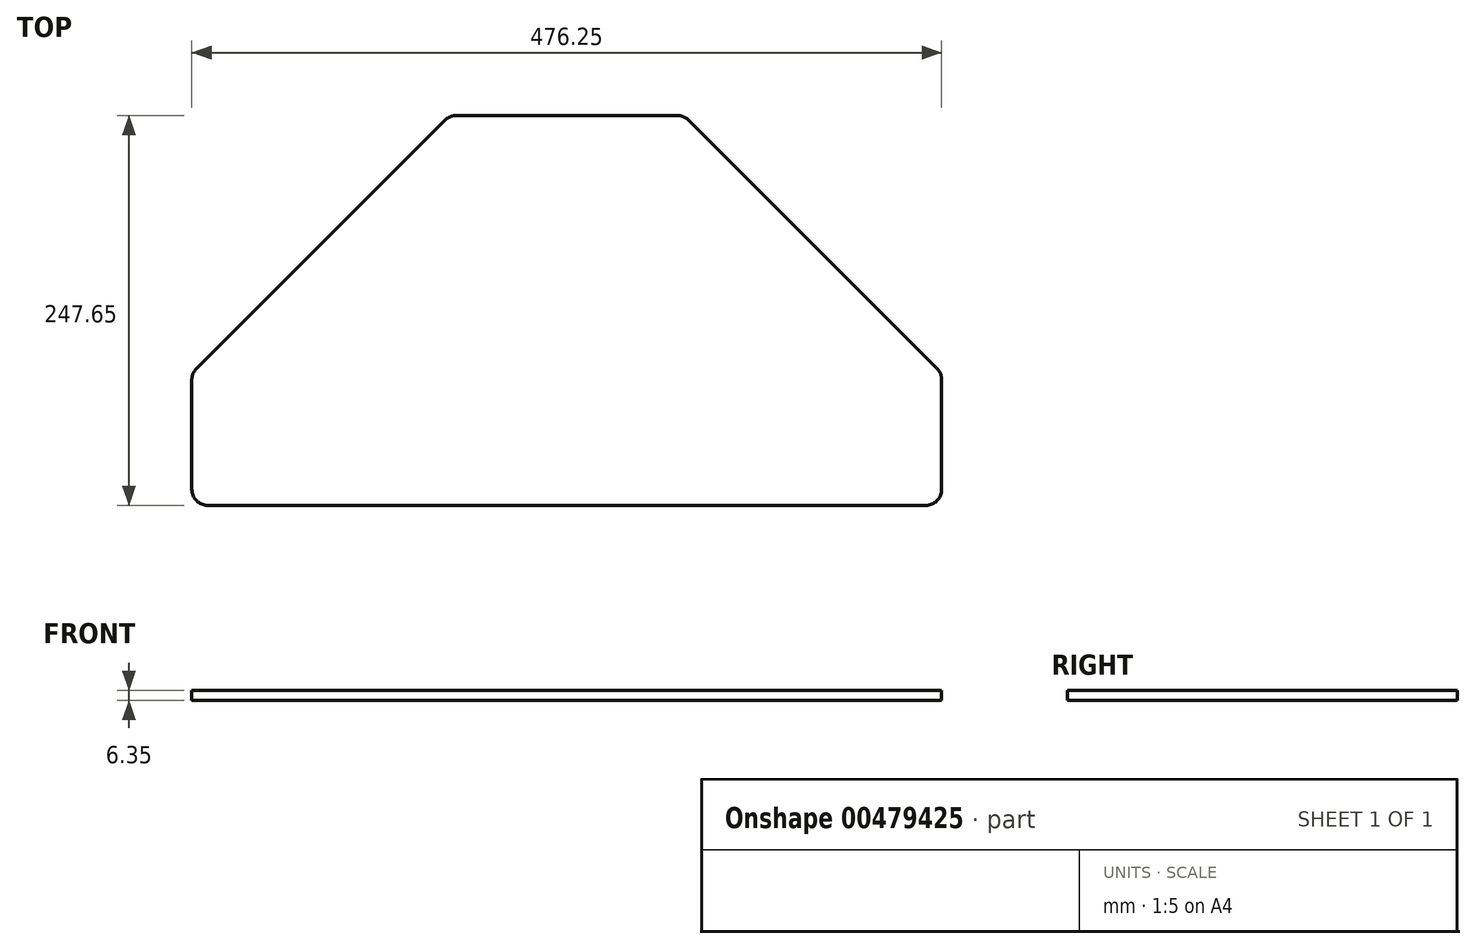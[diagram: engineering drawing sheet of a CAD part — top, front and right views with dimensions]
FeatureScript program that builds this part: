
annotation { "Feature Type Name" : "Feature", "Feature Type Description" : "" }
export const myFeature = defineFeature(function(context is Context, id is Id, definition is map)
    precondition{}
    {
        {
            var Q0;
            Q0=qCreatedBy(makeId("Top.planeOp"),FACE);
            var sketch = newSketch(context, id + "F0", { "sketchPlane" : qUnion([Q0]), "disableImprinting" : false});
            skLineSegment(sketch, "E0.bottom", {"start": v(0, 0) * mm, "end": v(476.25, 0) * mm});
            skLineSegment(sketch, "E0.top", {"start": v(0, 247.65) * mm, "end": v(476.25, 247.65) * mm});
            skLineSegment(sketch, "E0.left", {"start": v(0, 0) * mm, "end": v(0, 247.65) * mm});
            skLineSegment(sketch, "E0.right", {"start": v(476.25, 0) * mm, "end": v(476.25, 247.65) * mm});
            skLineSegment(sketch, "E1", {"start": v(0, 83.95) * mm, "end": v(476.25, 83.95) * mm});
            skPoint(sketch, "E2", {"position": v(163.7, 247.65) * mm});
            skPoint(sketch, "E3", {"position": v(312.55, 247.65) * mm});
            skLineSegment(sketch, "E4", {"start": v(0, 83.95) * mm, "end": v(163.7, 247.65) * mm});
            skLineSegment(sketch, "E5", {"start": v(312.55, 247.65) * mm, "end": v(476.25, 83.95) * mm});
            skSolve(sketch);
        }
        {
            var Q0;
            Q0=makeQuery(id+"F0.imprint","IMPRINT",FACE,{"disambiguationData":[TD([[makeQuery(id+"F0.imprint","IMPRINT",EDGE,{"derivedFrom":sQuery(id+"F0.wireOp",EDGE,"E1")}),1.0]])]});
            var Q1;
            {var subQ0=sQuery(id+"F0.wireOp",EDGE,"E0.bottom");Q1=makeQuery(id+"F0.imprint","IMPRINT",FACE,{"disambiguationData":[TD([[makeQuery(id+"F0.imprint","IMPRINT",EDGE,{"derivedFrom":subQ0}),1.0]])]});}
            extrude(context, id + "F1", {"entities" : qUnion([Q0, Q1]), "depth" : 6.35 * mm});
        }
        {
            var Q0;
            Q0=makeQuery(id+"F1.opExtrude","SWEPT_EDGE",EDGE,{"disambiguationData":[OSD([sQuery(id+"F0.wireOp",EDGE,"E0.top"),sQuery(id+"F0.wireOp",EDGE,"E4")])]});
            var Q1;
            Q1=makeQuery(id+"F1.opExtrude","SWEPT_EDGE",EDGE,{"disambiguationData":[OSD([sQuery(id+"F0.wireOp",EDGE,"E0.top"),sQuery(id+"F0.wireOp",EDGE,"E5")])]});
            var Q2;
            Q2=makeQuery(id+"F1.opExtrude","SWEPT_EDGE",EDGE,{"disambiguationData":[OSD([sQuery(id+"F0.wireOp",EDGE,"E0.right"),sQuery(id+"F0.wireOp",EDGE,"E1"),sQuery(id+"F0.wireOp",EDGE,"E5")])]});
            var Q3;
            Q3=makeQuery(id+"F1.opExtrude","SWEPT_EDGE",EDGE,{"disambiguationData":[OSD([sQuery(id+"F0.wireOp",EDGE,"E0.bottom"),sQuery(id+"F0.wireOp",EDGE,"E0.right")])]});
            var Q4;
            Q4=makeQuery(id+"F1.opExtrude","SWEPT_EDGE",EDGE,{"disambiguationData":[OSD([sQuery(id+"F0.wireOp",EDGE,"E0.bottom"),sQuery(id+"F0.wireOp",EDGE,"E0.left")])]});
            var Q5;
            Q5=makeQuery(id+"F1.opExtrude","SWEPT_EDGE",EDGE,{"disambiguationData":[OSD([sQuery(id+"F0.wireOp",EDGE,"E0.left"),sQuery(id+"F0.wireOp",EDGE,"E1"),sQuery(id+"F0.wireOp",EDGE,"E4")])]});
            fillet(context, id + "F2", {"entities" : qUnion([Q0, Q1, Q2, Q3, Q4, Q5]), "radius" : 10.16 * mm, "tangentPropagation" : true, "allowEdgeOverflow" : false});
        }
    });
